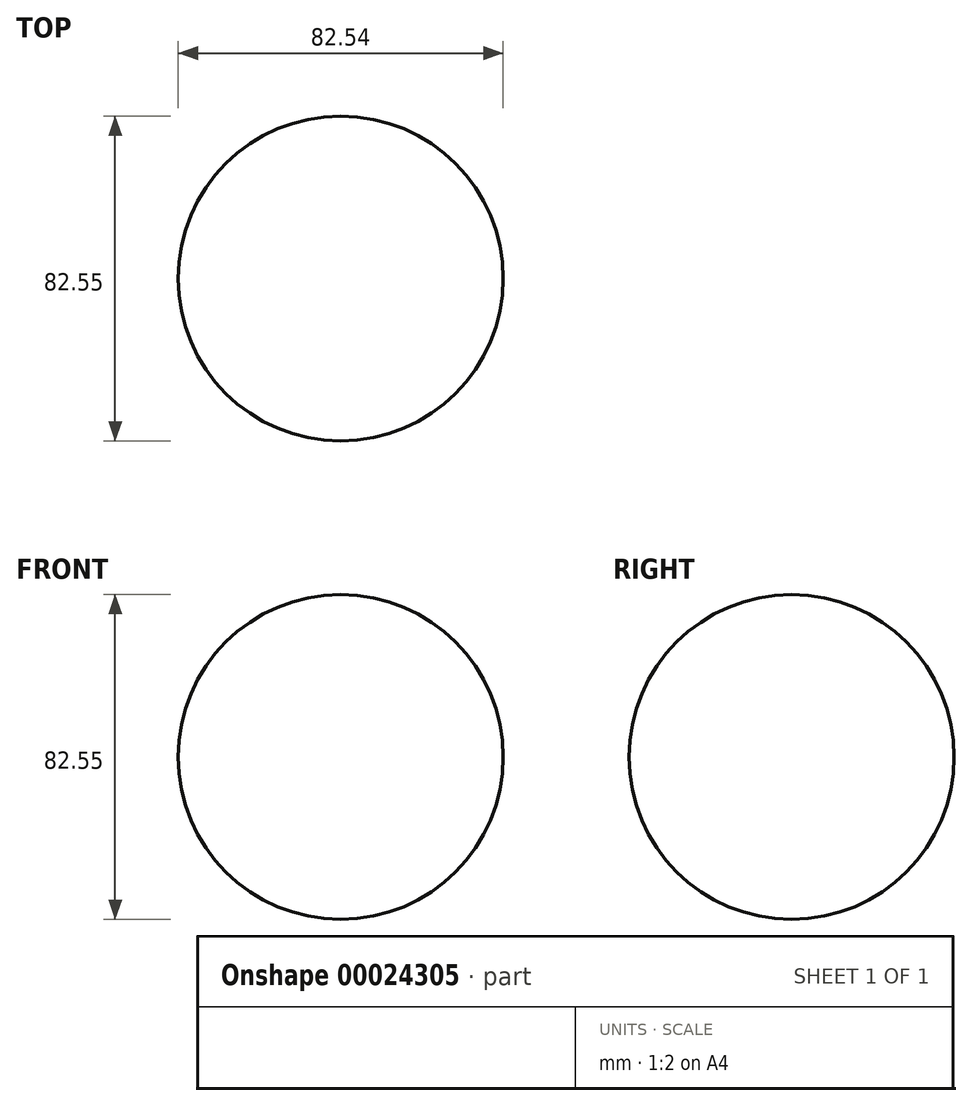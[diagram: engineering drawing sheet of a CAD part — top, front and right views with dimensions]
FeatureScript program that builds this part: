
annotation { "Feature Type Name" : "Feature", "Feature Type Description" : "" }
export const myFeature = defineFeature(function(context is Context, id is Id, definition is map)
    precondition{}
    {
        {
            var Q0;
            Q0=qCreatedBy(makeId("Right.planeOp"),FACE);
            var sketch = newSketch(context, id + "F0", { "sketchPlane" : qUnion([Q0])});
            skLineSegment(sketch, "E0", {"start": v(0, 0) * mm, "end": v(0, 82.55) * mm});
            skArc(sketch, "E1", {"start": v(0, 0) * mm, "mid": v(41.28, 41.27) * mm, "end": v(0, 82.55) * mm});
            skSolve(sketch);
        }
        {
            var Q0;
            Q0=makeQuery(id+"F0.imprint","IMPRINT",FACE,{"disambiguationData":[TD([[makeQuery(id+"F0.imprint","IMPRINT",EDGE,{"derivedFrom":sQuery(id+"F0.wireOp",EDGE,"E0")}),-1.0]])]});
            var Q1;
            Q1=sQuery(id+"F0.wireOp",EDGE,"E0");
            revolve(context, id + "F1", {"entities" : qUnion([Q0]), "axis" : qUnion([Q1]), "revolveType" : RevolveType.FULL});
        }
    });
